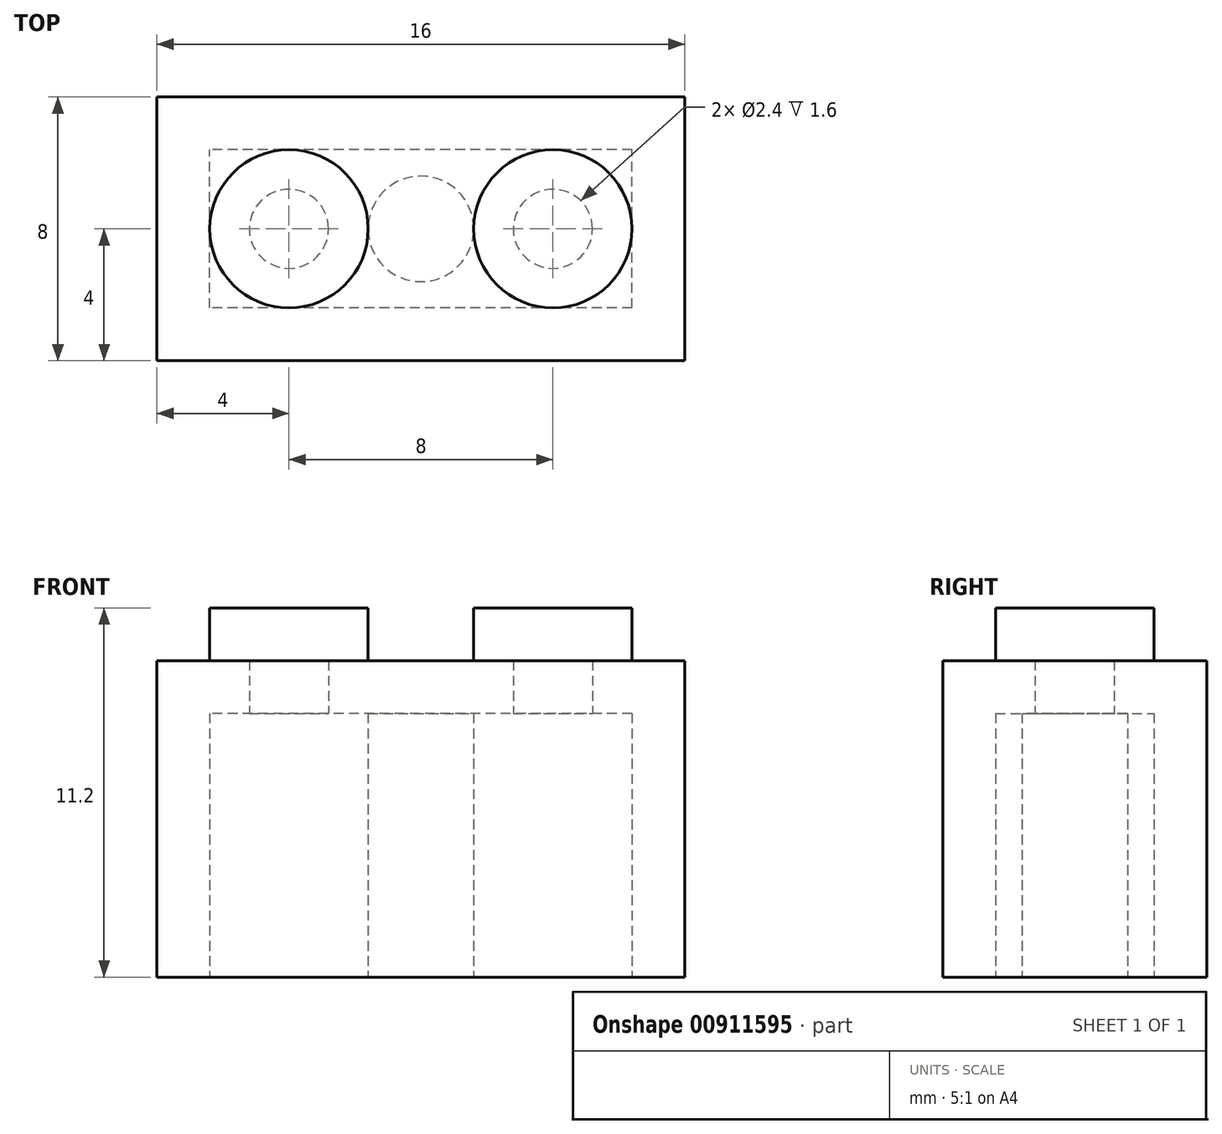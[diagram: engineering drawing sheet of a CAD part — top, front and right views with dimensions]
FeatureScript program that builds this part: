
annotation { "Feature Type Name" : "Feature", "Feature Type Description" : "" }
export const myFeature = defineFeature(function(context is Context, id is Id, definition is map)
    precondition{}
    {
        {
            var Q0;
            Q0=qCreatedBy(makeId("Top.planeOp"),FACE);
            var sketch = newSketch(context, id + "F0", { "sketchPlane" : qUnion([Q0])});
            skLineSegment(sketch, "E0.bottom", {"start": v(8, 4) * mm, "end": v(-8, 4) * mm});
            skLineSegment(sketch, "E0.top", {"start": v(8, -4) * mm, "end": v(-8, -4) * mm});
            skLineSegment(sketch, "E0.left", {"start": v(8, 4) * mm, "end": v(8, -4) * mm});
            skLineSegment(sketch, "E0.right", {"start": v(-8, 4) * mm, "end": v(-8, -4) * mm});
            skPoint(sketch, "E0.middle", {"position": v(0, 0) * mm});
            skSolve(sketch);
        }
        {
            var Q0;
            Q0=makeQuery(id+"F0.imprint","IMPRINT",FACE,{"disambiguationData":[TD([[makeQuery(id+"F0.imprint","IMPRINT",EDGE,{"derivedFrom":sQuery(id+"F0.wireOp",EDGE,"E0.bottom")}),1.0]])]});
            extrude(context, id + "F1", {"entities" : qUnion([Q0]), "depth" : 9.6 * mm, "offsetDistance" : 25 * mm});
        }
        {
            var Q0;
            Q0=makeQuery(id+"F1.opExtrude","CAP_FACE",FACE,{"disambiguationData":[OSD([sQuery(id+"F0.wireOp",EDGE,"E0.bottom"),sQuery(id+"F0.wireOp",EDGE,"E0.top"),sQuery(id+"F0.wireOp",EDGE,"E0.left"),sQuery(id+"F0.wireOp",EDGE,"E0.right")])],"isStart":true});
            var sketch = newSketch(context, id + "F2", { "sketchPlane" : qUnion([Q0])});
            skLineSegment(sketch, "E1.bottom", {"start": v(6.4, 2.4) * mm, "end": v(-6.4, 2.4) * mm});
            skLineSegment(sketch, "E1.top", {"start": v(6.4, -2.4) * mm, "end": v(-6.4, -2.4) * mm});
            skLineSegment(sketch, "E1.left", {"start": v(6.4, 2.4) * mm, "end": v(6.4, -2.4) * mm});
            skLineSegment(sketch, "E1.right", {"start": v(-6.4, 2.4) * mm, "end": v(-6.4, -2.4) * mm});
            skPoint(sketch, "E1.middle", {"position": v(0, 0) * mm});
            skCircle(sketch, "E2", {"center": v(0, 0) * mm, "radius": 1.6 * mm});
            skLineSegment(sketch, "E3", {"start": v(-1.6, 2.4) * mm, "end": v(-1.6, -2.4) * mm, "construction": true});
            skSolve(sketch);
        }
        {
            var Q0;
            Q0=makeQuery(id+"F2.imprint","IMPRINT",FACE,{"disambiguationData":[TD([[makeQuery(id+"F2.imprint","IMPRINT",EDGE,{"derivedFrom":sQuery(id+"F2.wireOp",EDGE,"E1.bottom")}),1.0]])]});
            extrude(context, id + "F3", {"entities" : qUnion([Q0]), "operationType" : NewBodyOperationType.REMOVE, "oppositeDirection" : true, "depth" : 8 * mm, "offsetDistance" : 25 * mm});
        }
        {
            var Q0;
            Q0=makeQuery(id+"F1.opExtrude","CAP_FACE",FACE,{"disambiguationData":[OSD([sQuery(id+"F0.wireOp",EDGE,"E0.bottom"),sQuery(id+"F0.wireOp",EDGE,"E0.top"),sQuery(id+"F0.wireOp",EDGE,"E0.left"),sQuery(id+"F0.wireOp",EDGE,"E0.right")])],"isStart":false});
            var sketch = newSketch(context, id + "F4", { "sketchPlane" : qUnion([Q0])});
            skCircle(sketch, "E4", {"center": v(-4, 0) * mm, "radius": 2.4 * mm});
            skCircle(sketch, "E5", {"center": v(4, 0) * mm, "radius": 2.4 * mm});
            skSolve(sketch);
        }
        {
            var Q0;
            Q0=makeQuery(id+"F4.imprint","IMPRINT",FACE,{"disambiguationData":[TD([[makeQuery(id+"F4.imprint","IMPRINT",EDGE,{"derivedFrom":sQuery(id+"F4.wireOp",EDGE,"E4")}),1.0]])]});
            var Q1;
            Q1=makeQuery(id+"F4.imprint","IMPRINT",FACE,{"disambiguationData":[TD([[makeQuery(id+"F4.imprint","IMPRINT",EDGE,{"derivedFrom":sQuery(id+"F4.wireOp",EDGE,"E5")}),1.0]])]});
            extrude(context, id + "F5", {"entities" : qUnion([Q0, Q1]), "operationType" : NewBodyOperationType.ADD, "depth" : 1.6 * mm, "offsetDistance" : 25 * mm});
        }
        {
            var Q0;
            Q0=makeQuery(id+"F3.boolean.opBoolean","COPY",FACE,{"derivedFrom":makeQuery(id+"F3.opExtrude","CAP_FACE",FACE,{"disambiguationData":[OSD([sQuery(id+"F2.wireOp",EDGE,"E1.bottom"),sQuery(id+"F2.wireOp",EDGE,"E1.top"),sQuery(id+"F2.wireOp",EDGE,"E1.left"),sQuery(id+"F2.wireOp",EDGE,"E1.right")])],"isStart":false})});
            var sketch = newSketch(context, id + "F6", { "sketchPlane" : qUnion([Q0])});
            skCircle(sketch, "E6", {"center": v(-4, 0) * mm, "radius": 1.2 * mm});
            skCircle(sketch, "E7", {"center": v(4, 0) * mm, "radius": 1.2 * mm});
            skSolve(sketch);
        }
        {
            var Q0;
            Q0=makeQuery(id+"F6.imprint","IMPRINT",FACE,{"disambiguationData":[TD([[makeQuery(id+"F6.imprint","IMPRINT",EDGE,{"derivedFrom":sQuery(id+"F6.wireOp",EDGE,"E7")}),1.0]])]});
            var Q1;
            Q1=makeQuery(id+"F6.imprint","IMPRINT",FACE,{"disambiguationData":[TD([[makeQuery(id+"F6.imprint","IMPRINT",EDGE,{"derivedFrom":sQuery(id+"F6.wireOp",EDGE,"E6")}),1.0]])]});
            extrude(context, id + "F7", {"entities" : qUnion([Q0, Q1]), "operationType" : NewBodyOperationType.REMOVE, "oppositeDirection" : true, "depth" : 1.6 * mm, "offsetDistance" : 25 * mm});
        }
    });
